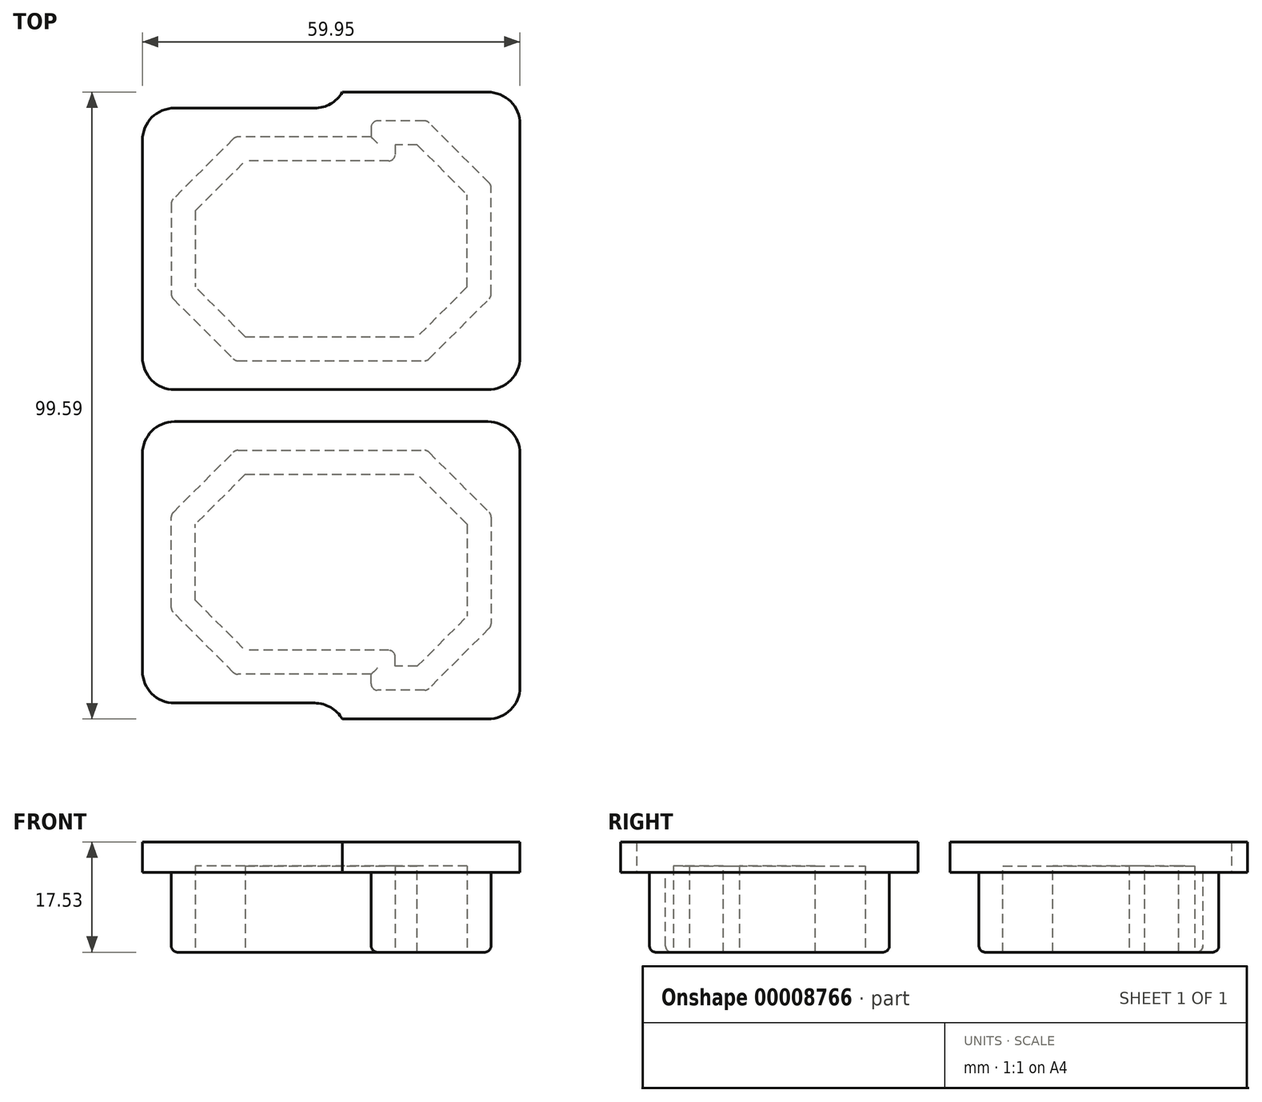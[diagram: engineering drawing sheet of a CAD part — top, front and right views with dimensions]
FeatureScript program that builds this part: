
annotation { "Feature Type Name" : "Feature", "Feature Type Description" : "" }
export const myFeature = defineFeature(function(context is Context, id is Id, definition is map)
    precondition{}
    {
        {
            var Q0;
            Q0=qCreatedBy(makeId("Top.planeOp"),FACE);
            var sketch = newSketch(context, id + "F0", { "sketchPlane" : qUnion([Q0])});
            skLineSegment(sketch, "E0", {"start": v(-19.94, 21.23) * mm, "end": v(30.86, 21.23) * mm});
            skLineSegment(sketch, "E1", {"start": v(30.86, 21.23) * mm, "end": v(30.86, -16.87) * mm});
            skLineSegment(sketch, "E2", {"start": v(30.86, -16.87) * mm, "end": v(11.8, -16.87) * mm});
            skLineSegment(sketch, "E3", {"start": v(11.8, -16.87) * mm, "end": v(11.8, -14.33) * mm});
            skLineSegment(sketch, "E4", {"start": v(11.8, -14.33) * mm, "end": v(-19.94, -14.33) * mm});
            skLineSegment(sketch, "E5", {"start": v(-19.94, -14.33) * mm, "end": v(-19.94, -14.33) * mm});
            skLineSegment(sketch, "E6", {"start": v(-19.94, -14.33) * mm, "end": v(-19.94, 21.23) * mm});
            skSolve(sketch);
        }
        {
            var Q0;
            Q0 = qSketchRegion(id + "F0", true);
            extrude(context, id + "F1", {"entities" : qUnion([Q0]), "depth" : 12.7 * mm});
        }
        {
            var Q0;
            Q0=makeQuery(id+"F1.opExtrude","CAP_FACE",FACE,{"disambiguationData":[OSD([sQuery(id+"F0.wireOp",EDGE,"E0"),sQuery(id+"F0.wireOp",EDGE,"E1"),sQuery(id+"F0.wireOp",EDGE,"E2"),sQuery(id+"F0.wireOp",EDGE,"E3"),sQuery(id+"F0.wireOp",EDGE,"E4"),sQuery(id+"F0.wireOp",EDGE,"E6")])],"isStart":false});
            var sketch = newSketch(context, id + "F2", { "sketchPlane" : qUnion([Q0])});
            skLineSegment(sketch, "E7.0", {"start": v(-24.52, 25.8) * mm, "end": v(35.43, 25.8) * mm});
            skLineSegment(sketch, "E7.1", {"start": v(-24.52, -18.9) * mm, "end": v(-24.52, 25.8) * mm});
            skLineSegment(sketch, "E7.2", {"start": v(7.23, -18.9) * mm, "end": v(-24.52, -18.9) * mm});
            skLineSegment(sketch, "E7.3", {"start": v(7.23, -21.45) * mm, "end": v(7.23, -18.9) * mm});
            skLineSegment(sketch, "E7.4", {"start": v(35.43, -21.45) * mm, "end": v(7.23, -21.45) * mm});
            skLineSegment(sketch, "E7.5", {"start": v(35.43, 25.8) * mm, "end": v(35.43, -21.45) * mm});
            skSolve(sketch);
        }
        {
            var Q0;
            Q0 = qSketchRegion(id + "F2", true);
            extrude(context, id + "F3", {"entities" : qUnion([Q0]), "operationType" : NewBodyOperationType.ADD, "depth" : 4.83 * mm});
        }
        {
            var Q0;
            Q0=makeQuery(id+"F3.opExtrude","SWEPT_EDGE",EDGE,{"disambiguationData":[OSD([sQuery(id+"F2.wireOp",EDGE,"E7.0"),sQuery(id+"F2.wireOp",EDGE,"E7.1")])]});
            var Q1;
            Q1=makeQuery(id+"F3.opExtrude","SWEPT_EDGE",EDGE,{"disambiguationData":[OSD([sQuery(id+"F2.wireOp",EDGE,"E7.0"),sQuery(id+"F2.wireOp",EDGE,"E7.5")])]});
            var Q2;
            Q2=makeQuery(id+"F3.opExtrude","SWEPT_EDGE",EDGE,{"disambiguationData":[OSD([sQuery(id+"F2.wireOp",EDGE,"E7.4"),sQuery(id+"F2.wireOp",EDGE,"E7.5")])]});
            var Q3;
            Q3=makeQuery(id+"F3.opExtrude","SWEPT_EDGE",EDGE,{"disambiguationData":[OSD([sQuery(id+"F2.wireOp",EDGE,"E7.1"),sQuery(id+"F2.wireOp",EDGE,"E7.2")])]});
            var Q4;
            Q4=makeQuery(id+"F3.opExtrude","SWEPT_EDGE",EDGE,{"disambiguationData":[OSD([sQuery(id+"F2.wireOp",EDGE,"E7.2"),sQuery(id+"F2.wireOp",EDGE,"E7.3")])]});
            fillet(context, id + "F4", {"entities" : qUnion([Q0, Q1, Q2, Q3, Q4]), "radius" : 5.08 * mm, "tangentPropagation" : true, "allowEdgeOverflow" : false});
        }
        {
            var Q0;
            Q0=makeQuery(id+"F1.opExtrude","SWEPT_EDGE",EDGE,{"disambiguationData":[OSD([sQuery(id+"F0.wireOp",EDGE,"E4"),sQuery(id+"F0.wireOp",EDGE,"E6")])]});
            var Q1;
            Q1=makeQuery(id+"F1.opExtrude","SWEPT_EDGE",EDGE,{"disambiguationData":[OSD([sQuery(id+"F0.wireOp",EDGE,"E1"),sQuery(id+"F0.wireOp",EDGE,"E2")])]});
            var Q2;
            Q2=makeQuery(id+"F1.opExtrude","SWEPT_EDGE",EDGE,{"disambiguationData":[OSD([sQuery(id+"F0.wireOp",EDGE,"E0"),sQuery(id+"F0.wireOp",EDGE,"E1")])]});
            var Q3;
            Q3=makeQuery(id+"F1.opExtrude","SWEPT_EDGE",EDGE,{"disambiguationData":[OSD([sQuery(id+"F0.wireOp",EDGE,"E0"),sQuery(id+"F0.wireOp",EDGE,"E6")])]});
            chamfer(context, id + "F5", {"entities" : qUnion([Q0, Q1, Q2, Q3]), "width" : 10.16 * mm, "tangentPropagation" : true});
        }
        {
            var Q0;
            Q0=makeQuery(id+"F1.opExtrude","CAP_FACE",FACE,{"disambiguationData":[OSD([sQuery(id+"F0.wireOp",EDGE,"E0"),sQuery(id+"F0.wireOp",EDGE,"E1"),sQuery(id+"F0.wireOp",EDGE,"E2"),sQuery(id+"F0.wireOp",EDGE,"E3"),sQuery(id+"F0.wireOp",EDGE,"E4"),sQuery(id+"F0.wireOp",EDGE,"E6")])],"isStart":true});
            shell(context, id + "F6", {"entities" : qUnion([Q0]), "thickness" : 3.8 * mm});
        }
        {
            var Q0;
            {var subQ0=sQuery(id+"F0.wireOp",EDGE,"E0");var subQ1=sQuery(id+"F0.wireOp",EDGE,"E1");Q0=makeQuery(id+"F5.opChamfer","BLEND_EDGE",EDGE,{"blendedFrom":[makeQuery(id+"F1.opExtrude","SWEPT_EDGE",EDGE,{"disambiguationData":[OSD([subQ0,subQ1])]}),makeQuery(id+"F1.opExtrude","CAP_FACE",FACE,{"disambiguationData":[OSD([subQ0,subQ1,sQuery(id+"F0.wireOp",EDGE,"E2"),sQuery(id+"F0.wireOp",EDGE,"E3"),sQuery(id+"F0.wireOp",EDGE,"E4"),sQuery(id+"F0.wireOp",EDGE,"E6")])],"isStart":true})],"blendedInto":[makeQuery(id+"F1.opExtrude","CAP_FACE",FACE,{"disambiguationData":[OSD([subQ0,subQ1,sQuery(id+"F0.wireOp",EDGE,"E2"),sQuery(id+"F0.wireOp",EDGE,"E3"),sQuery(id+"F0.wireOp",EDGE,"E4"),sQuery(id+"F0.wireOp",EDGE,"E6")])],"isStart":true})]});}
            var Q1;
            Q1=makeQuery(id+"F1.opExtrude","CAP_EDGE",EDGE,{"disambiguationData":[OSD([sQuery(id+"F0.wireOp",EDGE,"E1")])],"isStart":true});
            var Q2;
            Q2=makeQuery(id+"F1.opExtrude","CAP_EDGE",EDGE,{"disambiguationData":[OSD([sQuery(id+"F0.wireOp",EDGE,"E0")])],"isStart":true});
            var Q3;
            {var subQ0=sQuery(id+"F0.wireOp",EDGE,"E0");var subQ1=sQuery(id+"F0.wireOp",EDGE,"E6");Q3=makeQuery(id+"F5.opChamfer","BLEND_EDGE",EDGE,{"blendedFrom":[makeQuery(id+"F1.opExtrude","SWEPT_EDGE",EDGE,{"disambiguationData":[OSD([subQ0,subQ1])]}),makeQuery(id+"F1.opExtrude","CAP_FACE",FACE,{"disambiguationData":[OSD([subQ0,sQuery(id+"F0.wireOp",EDGE,"E1"),sQuery(id+"F0.wireOp",EDGE,"E2"),sQuery(id+"F0.wireOp",EDGE,"E3"),sQuery(id+"F0.wireOp",EDGE,"E4"),subQ1])],"isStart":true})],"blendedInto":[makeQuery(id+"F1.opExtrude","CAP_FACE",FACE,{"disambiguationData":[OSD([subQ0,sQuery(id+"F0.wireOp",EDGE,"E1"),sQuery(id+"F0.wireOp",EDGE,"E2"),sQuery(id+"F0.wireOp",EDGE,"E3"),sQuery(id+"F0.wireOp",EDGE,"E4"),subQ1])],"isStart":true})]});}
            var Q4;
            Q4=makeQuery(id+"F1.opExtrude","CAP_EDGE",EDGE,{"disambiguationData":[OSD([sQuery(id+"F0.wireOp",EDGE,"E6")])],"isStart":true});
            var Q5;
            {var subQ0=sQuery(id+"F0.wireOp",EDGE,"E4");var subQ1=sQuery(id+"F0.wireOp",EDGE,"E6");Q5=makeQuery(id+"F5.opChamfer","BLEND_EDGE",EDGE,{"blendedFrom":[makeQuery(id+"F1.opExtrude","SWEPT_EDGE",EDGE,{"disambiguationData":[OSD([subQ0,subQ1])]}),makeQuery(id+"F1.opExtrude","CAP_FACE",FACE,{"disambiguationData":[OSD([sQuery(id+"F0.wireOp",EDGE,"E0"),sQuery(id+"F0.wireOp",EDGE,"E1"),sQuery(id+"F0.wireOp",EDGE,"E2"),sQuery(id+"F0.wireOp",EDGE,"E3"),subQ0,subQ1])],"isStart":true})],"blendedInto":[makeQuery(id+"F1.opExtrude","CAP_FACE",FACE,{"disambiguationData":[OSD([sQuery(id+"F0.wireOp",EDGE,"E0"),sQuery(id+"F0.wireOp",EDGE,"E1"),sQuery(id+"F0.wireOp",EDGE,"E2"),sQuery(id+"F0.wireOp",EDGE,"E3"),subQ0,subQ1])],"isStart":true})]});}
            var Q6;
            Q6=makeQuery(id+"F1.opExtrude","CAP_EDGE",EDGE,{"disambiguationData":[OSD([sQuery(id+"F0.wireOp",EDGE,"E4")])],"isStart":true});
            var Q7;
            Q7=makeQuery(id+"F1.opExtrude","CAP_EDGE",EDGE,{"disambiguationData":[OSD([sQuery(id+"F0.wireOp",EDGE,"E3")])],"isStart":true});
            var Q8;
            Q8=makeQuery(id+"F1.opExtrude","CAP_EDGE",EDGE,{"disambiguationData":[OSD([sQuery(id+"F0.wireOp",EDGE,"E2")])],"isStart":true});
            var Q9;
            {var subQ0=sQuery(id+"F0.wireOp",EDGE,"E1");var subQ1=sQuery(id+"F0.wireOp",EDGE,"E2");Q9=makeQuery(id+"F5.opChamfer","BLEND_EDGE",EDGE,{"blendedFrom":[makeQuery(id+"F1.opExtrude","SWEPT_EDGE",EDGE,{"disambiguationData":[OSD([subQ0,subQ1])]}),makeQuery(id+"F1.opExtrude","CAP_FACE",FACE,{"disambiguationData":[OSD([sQuery(id+"F0.wireOp",EDGE,"E0"),subQ0,subQ1,sQuery(id+"F0.wireOp",EDGE,"E3"),sQuery(id+"F0.wireOp",EDGE,"E4"),sQuery(id+"F0.wireOp",EDGE,"E6")])],"isStart":true})],"blendedInto":[makeQuery(id+"F1.opExtrude","CAP_FACE",FACE,{"disambiguationData":[OSD([sQuery(id+"F0.wireOp",EDGE,"E0"),subQ0,subQ1,sQuery(id+"F0.wireOp",EDGE,"E3"),sQuery(id+"F0.wireOp",EDGE,"E4"),sQuery(id+"F0.wireOp",EDGE,"E6")])],"isStart":true})]});}
            var Q10;
            Q10=makeQuery(id+"F6.opShell","OFFSET_EDGE",EDGE,{"disambiguationData":[OSD([sQuery(id+"F0.wireOp",EDGE,"E3"),sQuery(id+"F0.wireOp",EDGE,"E4")])]});
            var Q11;
            {var subQ0=sQuery(id+"F0.wireOp",EDGE,"E1");Q11=makeQuery(id+"F5.opChamfer","BLEND_EDGE",EDGE,{"blendedFrom":[makeQuery(id+"F1.opExtrude","SWEPT_EDGE",EDGE,{"disambiguationData":[OSD([sQuery(id+"F0.wireOp",EDGE,"E0"),subQ0])]}),makeQuery(id+"F1.opExtrude","SWEPT_FACE",FACE,{"disambiguationData":[OSD([subQ0])]})],"blendedInto":[makeQuery(id+"F1.opExtrude","SWEPT_FACE",FACE,{"disambiguationData":[OSD([subQ0])]})]});}
            var Q12;
            {var subQ0=sQuery(id+"F0.wireOp",EDGE,"E0");Q12=makeQuery(id+"F5.opChamfer","BLEND_EDGE",EDGE,{"blendedFrom":[makeQuery(id+"F1.opExtrude","SWEPT_EDGE",EDGE,{"disambiguationData":[OSD([subQ0,sQuery(id+"F0.wireOp",EDGE,"E1")])]}),makeQuery(id+"F1.opExtrude","SWEPT_FACE",FACE,{"disambiguationData":[OSD([subQ0])]})],"blendedInto":[makeQuery(id+"F1.opExtrude","SWEPT_FACE",FACE,{"disambiguationData":[OSD([subQ0])]})]});}
            var Q13;
            {var subQ0=sQuery(id+"F0.wireOp",EDGE,"E0");Q13=makeQuery(id+"F5.opChamfer","BLEND_EDGE",EDGE,{"blendedFrom":[makeQuery(id+"F1.opExtrude","SWEPT_EDGE",EDGE,{"disambiguationData":[OSD([subQ0,sQuery(id+"F0.wireOp",EDGE,"E6")])]}),makeQuery(id+"F1.opExtrude","SWEPT_FACE",FACE,{"disambiguationData":[OSD([subQ0])]})],"blendedInto":[makeQuery(id+"F1.opExtrude","SWEPT_FACE",FACE,{"disambiguationData":[OSD([subQ0])]})]});}
            var Q14;
            {var subQ0=sQuery(id+"F0.wireOp",EDGE,"E1");Q14=makeQuery(id+"F5.opChamfer","BLEND_EDGE",EDGE,{"blendedFrom":[makeQuery(id+"F1.opExtrude","SWEPT_EDGE",EDGE,{"disambiguationData":[OSD([subQ0,sQuery(id+"F0.wireOp",EDGE,"E2")])]}),makeQuery(id+"F1.opExtrude","SWEPT_FACE",FACE,{"disambiguationData":[OSD([subQ0])]})],"blendedInto":[makeQuery(id+"F1.opExtrude","SWEPT_FACE",FACE,{"disambiguationData":[OSD([subQ0])]})]});}
            var Q15;
            {var subQ0=sQuery(id+"F0.wireOp",EDGE,"E2");Q15=makeQuery(id+"F5.opChamfer","BLEND_EDGE",EDGE,{"blendedFrom":[makeQuery(id+"F1.opExtrude","SWEPT_EDGE",EDGE,{"disambiguationData":[OSD([sQuery(id+"F0.wireOp",EDGE,"E1"),subQ0])]}),makeQuery(id+"F1.opExtrude","SWEPT_FACE",FACE,{"disambiguationData":[OSD([subQ0])]})],"blendedInto":[makeQuery(id+"F1.opExtrude","SWEPT_FACE",FACE,{"disambiguationData":[OSD([subQ0])]})]});}
            var Q16;
            Q16=makeQuery(id+"F1.opExtrude","SWEPT_EDGE",EDGE,{"disambiguationData":[OSD([sQuery(id+"F0.wireOp",EDGE,"E2"),sQuery(id+"F0.wireOp",EDGE,"E3")])]});
            var Q17;
            {var subQ0=sQuery(id+"F0.wireOp",EDGE,"E4");Q17=makeQuery(id+"F5.opChamfer","BLEND_EDGE",EDGE,{"blendedFrom":[makeQuery(id+"F1.opExtrude","SWEPT_EDGE",EDGE,{"disambiguationData":[OSD([subQ0,sQuery(id+"F0.wireOp",EDGE,"E6")])]}),makeQuery(id+"F1.opExtrude","SWEPT_FACE",FACE,{"disambiguationData":[OSD([subQ0])]})],"blendedInto":[makeQuery(id+"F1.opExtrude","SWEPT_FACE",FACE,{"disambiguationData":[OSD([subQ0])]})]});}
            var Q18;
            {var subQ0=sQuery(id+"F0.wireOp",EDGE,"E6");Q18=makeQuery(id+"F5.opChamfer","BLEND_EDGE",EDGE,{"blendedFrom":[makeQuery(id+"F1.opExtrude","SWEPT_EDGE",EDGE,{"disambiguationData":[OSD([sQuery(id+"F0.wireOp",EDGE,"E4"),subQ0])]}),makeQuery(id+"F1.opExtrude","SWEPT_FACE",FACE,{"disambiguationData":[OSD([subQ0])]})],"blendedInto":[makeQuery(id+"F1.opExtrude","SWEPT_FACE",FACE,{"disambiguationData":[OSD([subQ0])]})]});}
            var Q19;
            {var subQ0=sQuery(id+"F0.wireOp",EDGE,"E6");Q19=makeQuery(id+"F5.opChamfer","BLEND_EDGE",EDGE,{"blendedFrom":[makeQuery(id+"F1.opExtrude","SWEPT_EDGE",EDGE,{"disambiguationData":[OSD([sQuery(id+"F0.wireOp",EDGE,"E0"),subQ0])]}),makeQuery(id+"F1.opExtrude","SWEPT_FACE",FACE,{"disambiguationData":[OSD([subQ0])]})],"blendedInto":[makeQuery(id+"F1.opExtrude","SWEPT_FACE",FACE,{"disambiguationData":[OSD([subQ0])]})]});}
            fillet(context, id + "F7", {"entities" : qUnion([Q0, Q1, Q2, Q3, Q4, Q5, Q6, Q7, Q8, Q9, Q10, Q11, Q12, Q13, Q14, Q15, Q16, Q17, Q18, Q19]), "radius" : 1.02 * mm, "tangentPropagation" : true, "allowEdgeOverflow" : false});
        }
        {
            var Q0;
            Q0=makeQuery(id+"F6.opShell","OFFSET_FACE",FACE,{"disambiguationData":[OSD([sQuery(id+"F2.wireOp",EDGE,"E7.0"),sQuery(id+"F2.wireOp",EDGE,"E7.1"),sQuery(id+"F2.wireOp",EDGE,"E7.2"),sQuery(id+"F2.wireOp",EDGE,"E7.3"),sQuery(id+"F2.wireOp",EDGE,"E7.4"),sQuery(id+"F2.wireOp",EDGE,"E7.5")])]});
            var sketch = newSketch(context, id + "F8", { "sketchPlane" : qUnion([Q0])});
            skLineSegment(sketch, "E8.0", {"start": v(-8.2, 10.52) * mm, "end": v(-16.13, 2.6) * mm});
            skLineSegment(sketch, "E8.1", {"start": v(14.6, 10.52) * mm, "end": v(-8.2, 10.52) * mm});
            skArc(sketch, "E8.2", {"start": v(14.6, 10.52) * mm, "mid": v(15.32, 10.82) * mm, "end": v(15.62, 11.54) * mm});
            skLineSegment(sketch, "E8.3", {"start": v(15.62, 13.06) * mm, "end": v(15.62, 11.54) * mm});
            skLineSegment(sketch, "E8.4", {"start": v(19.12, 13.06) * mm, "end": v(15.62, 13.06) * mm});
            skLineSegment(sketch, "E8.5", {"start": v(27.05, 5.13) * mm, "end": v(19.12, 13.06) * mm});
            skLineSegment(sketch, "E8.6", {"start": v(27.05, -9.5) * mm, "end": v(27.05, 5.13) * mm});
            skLineSegment(sketch, "E8.7", {"start": v(19.12, -17.42) * mm, "end": v(27.05, -9.5) * mm});
            skLineSegment(sketch, "E8.8", {"start": v(-8.2, -17.42) * mm, "end": v(19.12, -17.42) * mm});
            skLineSegment(sketch, "E8.9", {"start": v(-16.13, -9.5) * mm, "end": v(-8.2, -17.42) * mm});
            skLineSegment(sketch, "E8.10", {"start": v(-16.13, 2.6) * mm, "end": v(-16.13, -9.5) * mm});
            skSolve(sketch);
        }
        {
            var Q0;
            Q0=makeQuery(id+"F3.opExtrude","SWEPT_FACE",FACE,{"disambiguationData":[OSD([sQuery(id+"F2.wireOp",EDGE,"E7.0")])]});
            cPlane(context, id + "F9", {"entities" : qUnion([Q0]), "cplaneType" : CPlaneType.OFFSET, "offset" : 2.54 * mm, "width" : 152.4 * mm, "height" : 152.4 * mm});
        }
        {
            var Q0;
            Q0=makeQuery(id+"F1.opExtrude","SWEPT_BODY",BODY,{"disambiguationData":[OSD([sQuery(id+"F0.wireOp",EDGE,"E0"),sQuery(id+"F0.wireOp",EDGE,"E1"),sQuery(id+"F0.wireOp",EDGE,"E2"),sQuery(id+"F0.wireOp",EDGE,"E3"),sQuery(id+"F0.wireOp",EDGE,"E4"),sQuery(id+"F0.wireOp",EDGE,"E6")])]});
            var Q1;
            Q1=qCreatedBy(id+"F9.planeOp",FACE);
            mirror(context, id + "F10", {"entities" : qUnion([Q0]), "mirrorPlane" : qUnion([Q1])});
        }
    });
